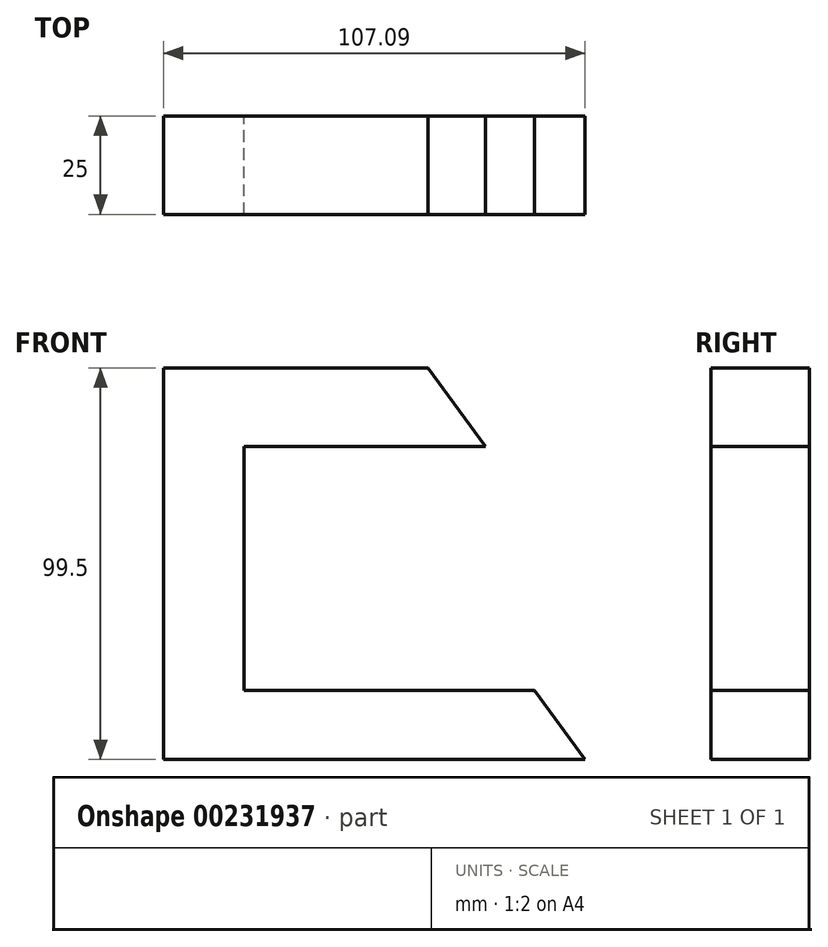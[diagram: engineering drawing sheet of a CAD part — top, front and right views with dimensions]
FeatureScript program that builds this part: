
annotation { "Feature Type Name" : "Feature", "Feature Type Description" : "" }
export const myFeature = defineFeature(function(context is Context, id is Id, definition is map)
    precondition{}
    {
        {
            var Q0;
            Q0=qCreatedBy(makeId("Front.planeOp"),FACE);
            var sketch = newSketch(context, id + "F0", { "sketchPlane" : qUnion([Q0])});
            skLineSegment(sketch, "E0", {"start": v(-67.18, 81.98) * mm, "end": v(-67.18, -14.9) * mm});
            skLineSegment(sketch, "E1", {"start": v(-67.18, -14.9) * mm, "end": v(-67.18, -17.52) * mm});
            skLineSegment(sketch, "E2", {"start": v(-67.18, -17.52) * mm, "end": v(0, -17.52) * mm});
            skLineSegment(sketch, "E3", {"start": v(-67.18, -17.52) * mm, "end": v(39.91, -17.52) * mm});
            skLineSegment(sketch, "E4", {"start": v(39.91, -17.52) * mm, "end": v(27.1, 0) * mm});
            skLineSegment(sketch, "E5", {"start": v(27.1, 0) * mm, "end": v(-67.18, 0) * mm});
            skLineSegment(sketch, "E6", {"start": v(-67.18, 0) * mm, "end": v(-46.67, 0) * mm});
            skLineSegment(sketch, "E7", {"start": v(-46.67, 0) * mm, "end": v(-46.67, 81.98) * mm});
            skLineSegment(sketch, "E8", {"start": v(-46.67, 81.98) * mm, "end": v(0, 81.98) * mm});
            skLineSegment(sketch, "E9", {"start": v(0, 81.98) * mm, "end": v(14.57, 62.07) * mm});
            skLineSegment(sketch, "E10", {"start": v(14.57, 62.07) * mm, "end": v(-46.67, 62.07) * mm});
            skLineSegment(sketch, "E11", {"start": v(-46.67, 62.07) * mm, "end": v(-67.18, 81.98) * mm});
            skLineSegment(sketch, "E12", {"start": v(-67.18, 81.98) * mm, "end": v(-46.67, 81.98) * mm});
            skSolve(sketch);
        }
        {
            var Q0;
            Q0 = qSketchRegion(id + "F0", true);
            extrude(context, id + "F1", {"entities" : qUnion([Q0]), "depth" : 25 * mm});
        }
    });
